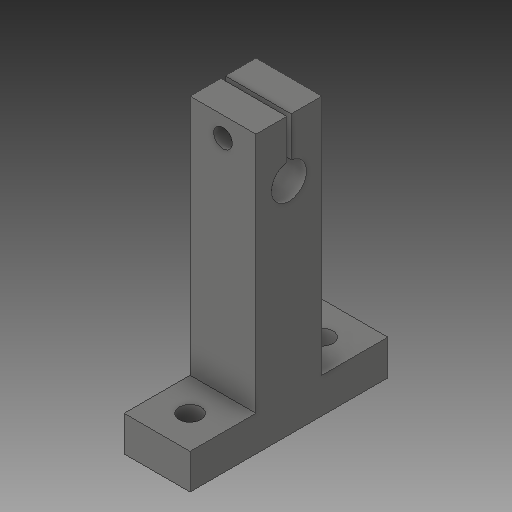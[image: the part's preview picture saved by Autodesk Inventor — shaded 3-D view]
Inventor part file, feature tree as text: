
AUTODESK INVENTOR PART (.ipt)
format: ipt  version: 2019 (Build 230136000, 136)  size: 142,336 bytes
history: native  units: mm
features: extrude x4, sketch x3, projected_geometry x2
ambient origin geometry x8: Origin, YZ Plane, XZ Plane, XY Plane, X Axis, Y Axis, Z Axis, Center Point
bodies: Solid1 (feature_tree)
feature tree (9):
  sketch  "Sketch1"  dims[d0=8.0mm d1=1.0mm]
  extrude  "Extrusion1"  Depth=1.0mm
  extrude  "Extrusion2"  Depth=15.0mm
  extrude  "Extrusion3"  Depth=8.0mm
  extrude  "Extrusion4"  Depth=15.0mm TaperAngle=0.0deg
  sketch  "Sketch2"  dims[d2=7.0mm d3=15.0mm]
  projected_geometry  "Projected Loop1"
  projected_geometry  "Projected Loop2"
  sketch  "Sketch3"  dims[d5=55.0mm d6=8.0mm d7=15.0mm d8=0.0mm d9=10.0mm d10=0.0mm d11=50.0mm d12=5.0mm d13=10.0mm d14=0.0mm d15=4.25mm d16=10.0mm d17=0.0mm]
